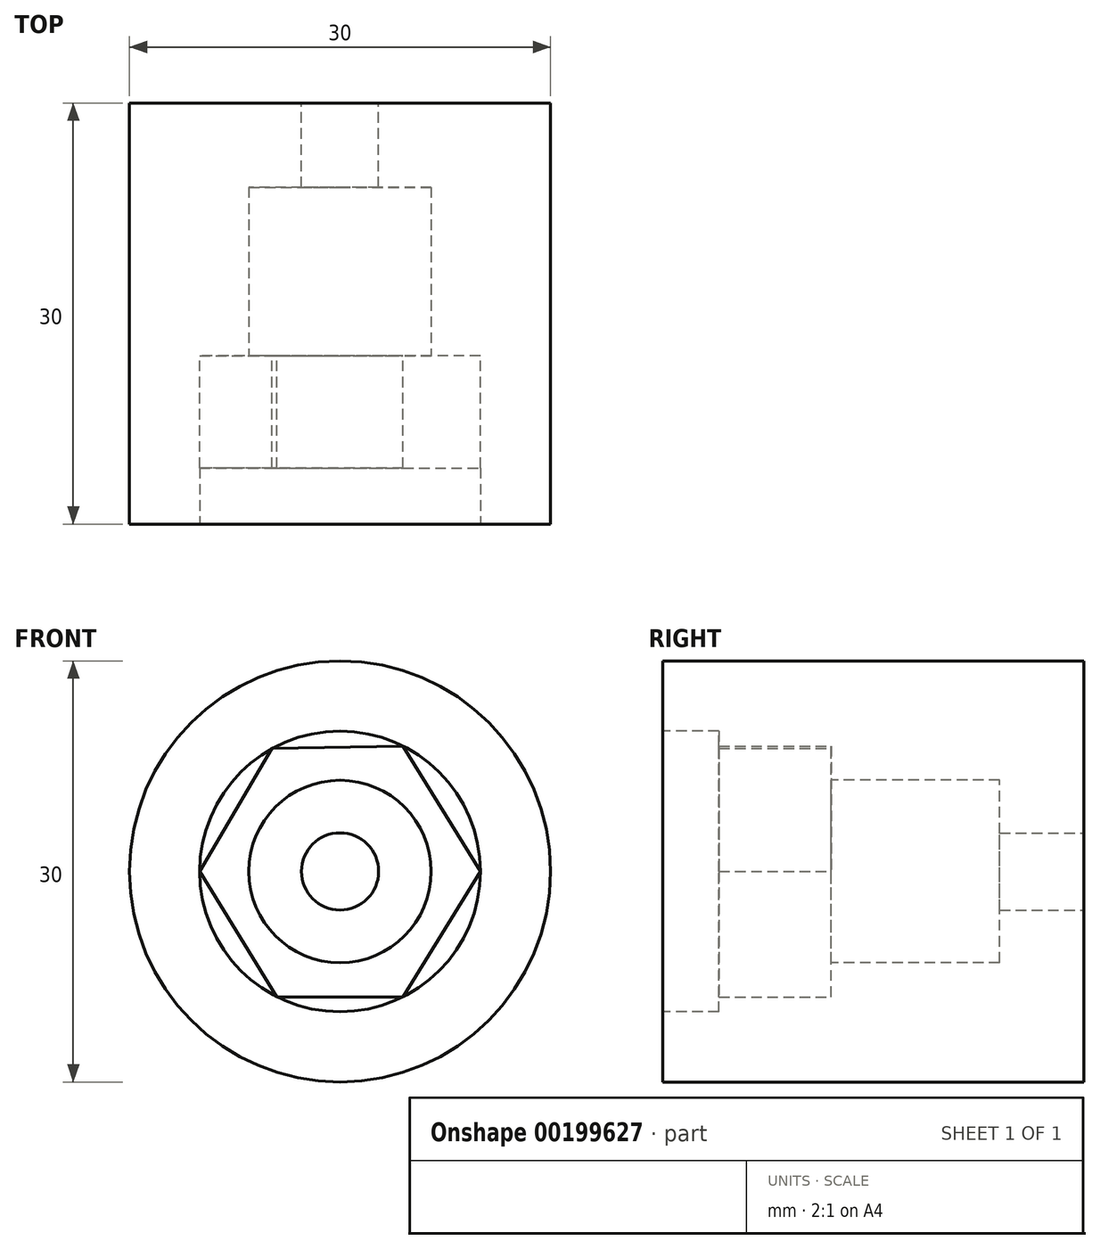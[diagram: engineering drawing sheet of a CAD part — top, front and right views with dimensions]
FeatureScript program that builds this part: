
annotation { "Feature Type Name" : "Feature", "Feature Type Description" : "" }
export const myFeature = defineFeature(function(context is Context, id is Id, definition is map)
    precondition{}
    {
        {
            var Q0;
            Q0=qCreatedBy(makeId("Front.planeOp"),FACE);
            var sketch = newSketch(context, id + "F0", { "sketchPlane" : qUnion([Q0])});
            skCircle(sketch, "E0", {"center": v(0, 0) * mm, "radius": 15 * mm});
            skCircle(sketch, "E1", {"center": v(0, 0) * mm, "radius": 2.75 * mm});
            skCircle(sketch, "E2", {"center": v(0, 0) * mm, "radius": 9.25 * mm});
            skCircle(sketch, "E3", {"center": v(0, 0) * mm, "radius": 4.5 * mm});
            skSolve(sketch);
        }
        {
            var Q0;
            Q0=makeQuery(id+"F0.imprint","IMPRINT",FACE,{"disambiguationData":[TD([[makeQuery(id+"F0.imprint","IMPRINT",EDGE,{"derivedFrom":sQuery(id+"F0.wireOp",EDGE,"E1")}),-1.0]])]});
            var Q1;
            Q1=makeQuery(id+"F0.imprint","IMPRINT",FACE,{"disambiguationData":[TD([[makeQuery(id+"F0.imprint","IMPRINT",EDGE,{"derivedFrom":sQuery(id+"F0.wireOp",EDGE,"E2")}),1.0]])]});
            var Q2;
            Q2=makeQuery(id+"F0.imprint","IMPRINT",FACE,{"disambiguationData":[TD([[makeQuery(id+"F0.imprint","IMPRINT",EDGE,{"derivedFrom":sQuery(id+"F0.wireOp",EDGE,"E0")}),1.0]])]});
            extrude(context, id + "F1", {"entities" : qUnion([Q0, Q1, Q2]), "depth" : 30 * mm});
        }
        {
            var Q0;
            Q0=makeQuery(id+"F1.opExtrude","CAP_FACE",FACE,{"disambiguationData":[OSD([sQuery(id+"F0.wireOp",EDGE,"E0"),sQuery(id+"F0.wireOp",EDGE,"E1")])],"isStart":false});
            var sketch = newSketch(context, id + "F2", { "sketchPlane" : qUnion([Q0])});
            skCircle(sketch, "E4", {"center": v(0, 0) * mm, "radius": 10 * mm});
            skSolve(sketch);
        }
        {
            var Q0;
            Q0=makeQuery(id+"F2.imprint","IMPRINT",FACE,{"disambiguationData":[TD([[makeQuery(id+"F2.imprint","IMPRINT",EDGE,{"derivedFrom":sQuery(id+"F2.wireOp",EDGE,"E4")}),1.0]])]});
            extrude(context, id + "F3", {"entities" : qUnion([Q0]), "operationType" : NewBodyOperationType.REMOVE, "oppositeDirection" : true, "depth" : 12 * mm});
        }
        {
            var Q0;
            Q0=makeQuery(id+"F3.boolean.opBoolean","COPY",FACE,{"derivedFrom":makeQuery(id+"F3.opExtrude","CAP_FACE",FACE,{"disambiguationData":[OSD([sQuery(id+"F0.wireOp",EDGE,"E1"),sQuery(id+"F2.wireOp",EDGE,"E4")])],"isStart":false})});
            var sketch = newSketch(context, id + "F4", { "sketchPlane" : qUnion([Q0])});
            skCircle(sketch, "E5", {"center": v(0, 0) * mm, "radius": 6.5 * mm});
            skSolve(sketch);
        }
        {
            var Q0;
            Q0=makeQuery(id+"F4.imprint","IMPRINT",FACE,{"disambiguationData":[TD([[makeQuery(id+"F4.imprint","IMPRINT",EDGE,{"derivedFrom":sQuery(id+"F4.wireOp",EDGE,"E5")}),1.0]])]});
            extrude(context, id + "F5", {"entities" : qUnion([Q0]), "operationType" : NewBodyOperationType.REMOVE, "oppositeDirection" : true, "depth" : 12 * mm});
        }
        {
            var Q0;
            Q0=makeQuery(id+"F3.boolean.opBoolean","COPY",FACE,{"derivedFrom":makeQuery(id+"F3.opExtrude","CAP_FACE",FACE,{"disambiguationData":[OSD([sQuery(id+"F0.wireOp",EDGE,"E1"),sQuery(id+"F2.wireOp",EDGE,"E4")])],"isStart":false})});
            var sketch = newSketch(context, id + "F6", { "sketchPlane" : qUnion([Q0])});
            skLineSegment(sketch, "E6", {"start": v(-4.84, 8.75) * mm, "end": v(4.5, 8.93) * mm});
            skLineSegment(sketch, "E7", {"start": v(4.5, 8.93) * mm, "end": v(10, 0) * mm});
            skLineSegment(sketch, "E8", {"start": v(10, 0) * mm, "end": v(4.5, -8.93) * mm});
            skLineSegment(sketch, "E9", {"start": v(4.5, -8.93) * mm, "end": v(-4.5, -8.93) * mm});
            skLineSegment(sketch, "E10", {"start": v(-4.5, -8.93) * mm, "end": v(-10, 0) * mm});
            skLineSegment(sketch, "E11", {"start": v(-10, 0) * mm, "end": v(-4.84, 8.75) * mm});
            skSolve(sketch);
        }
        {
            var Q0;
            {var subQ0=sQuery(id+"F6.wireOp",EDGE,"E6");Q0=makeQuery(id+"F6.imprint","IMPRINT",FACE,{"disambiguationData":[TD([[makeQuery(id+"F6.imprint","IMPRINT",EDGE,{"derivedFrom":subQ0}),1.0]])]});}
            var Q1;
            {var subQ0=sQuery(id+"F6.wireOp",EDGE,"E7");Q1=makeQuery(id+"F6.imprint","IMPRINT",FACE,{"disambiguationData":[TD([[makeQuery(id+"F6.imprint","IMPRINT",EDGE,{"derivedFrom":subQ0}),1.0]])]});}
            var Q2;
            {var subQ0=sQuery(id+"F6.wireOp",EDGE,"E8");Q2=makeQuery(id+"F6.imprint","IMPRINT",FACE,{"disambiguationData":[TD([[makeQuery(id+"F6.imprint","IMPRINT",EDGE,{"derivedFrom":subQ0}),1.0]])]});}
            var Q3;
            {var subQ0=sQuery(id+"F6.wireOp",EDGE,"E9");Q3=makeQuery(id+"F6.imprint","IMPRINT",FACE,{"disambiguationData":[TD([[makeQuery(id+"F6.imprint","IMPRINT",EDGE,{"derivedFrom":subQ0}),1.0]])]});}
            var Q4;
            {var subQ0=sQuery(id+"F6.wireOp",EDGE,"E10");Q4=makeQuery(id+"F6.imprint","IMPRINT",FACE,{"disambiguationData":[TD([[makeQuery(id+"F6.imprint","IMPRINT",EDGE,{"derivedFrom":subQ0}),1.0]])]});}
            var Q5;
            {var subQ0=sQuery(id+"F6.wireOp",EDGE,"E11");Q5=makeQuery(id+"F6.imprint","IMPRINT",FACE,{"disambiguationData":[TD([[makeQuery(id+"F6.imprint","IMPRINT",EDGE,{"derivedFrom":subQ0}),1.0]])]});}
            extrude(context, id + "F7", {"entities" : qUnion([Q0, Q1, Q2, Q3, Q4, Q5]), "operationType" : NewBodyOperationType.ADD, "depth" : 8 * mm});
        }
    });
